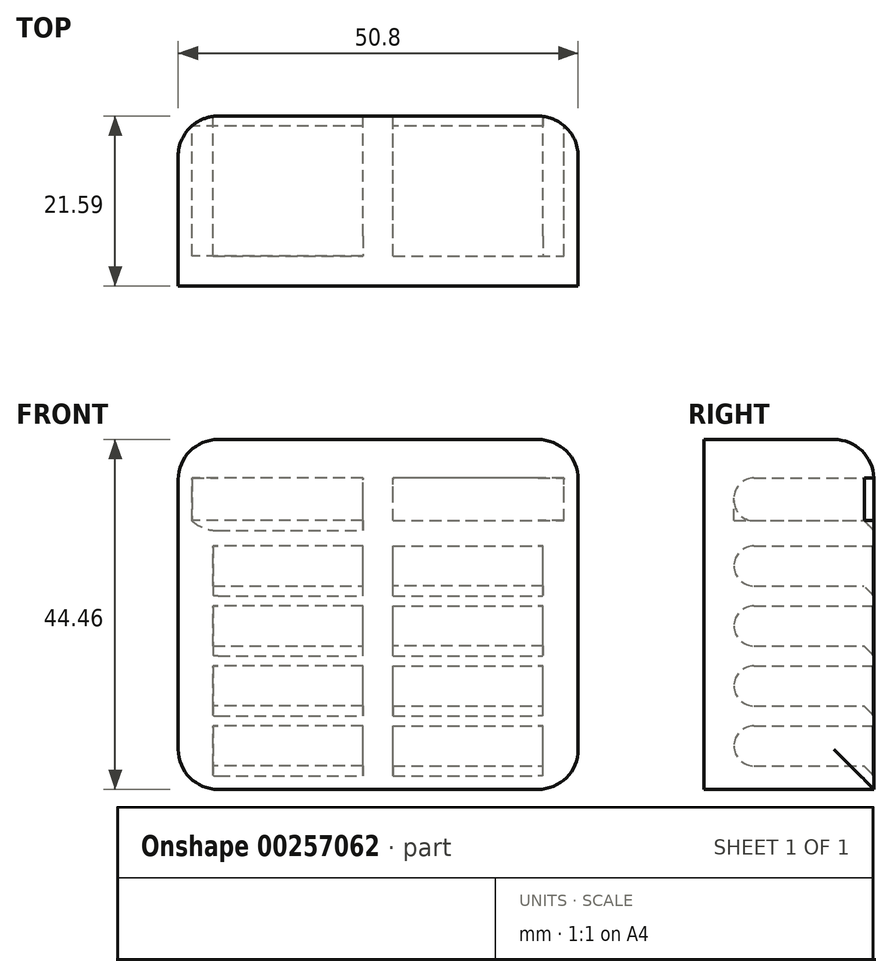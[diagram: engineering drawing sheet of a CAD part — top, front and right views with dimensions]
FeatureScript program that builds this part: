
annotation { "Feature Type Name" : "Feature", "Feature Type Description" : "" }
export const myFeature = defineFeature(function(context is Context, id is Id, definition is map)
    precondition{}
    {
        {
            var Q0;
            Q0=qCreatedBy(makeId("Front.planeOp"),FACE);
            var sketch = newSketch(context, id + "F0", { "sketchPlane" : qUnion([Q0])});
            skLineSegment(sketch, "E0.bottom", {"start": v(-25.4, -22.23) * mm, "end": v(25.4, -22.23) * mm});
            skLineSegment(sketch, "E0.top", {"start": v(-25.4, 22.23) * mm, "end": v(25.4, 22.23) * mm});
            skLineSegment(sketch, "E0.left", {"start": v(-25.4, -22.22) * mm, "end": v(-25.4, 22.22) * mm});
            skLineSegment(sketch, "E0.right", {"start": v(25.4, -22.23) * mm, "end": v(25.4, 22.22) * mm});
            skPoint(sketch, "E0.middle", {"position": v(0, 0) * mm});
            skLineSegment(sketch, "E1", {"start": v(-1.92, -19.23) * mm, "end": v(-1.92, -14.15) * mm});
            skLineSegment(sketch, "E2", {"start": v(-20.97, -19.23) * mm, "end": v(-20.97, -14.15) * mm});
            skLineSegment(sketch, "E3", {"start": v(-20.97, 3.63) * mm, "end": v(-1.92, 3.63) * mm});
            skLineSegment(sketch, "E4", {"start": v(-20.97, -4) * mm, "end": v(-1.92, -4) * mm});
            skLineSegment(sketch, "E5", {"start": v(-1.92, 1.09) * mm, "end": v(-20.97, 1.09) * mm});
            skLineSegment(sketch, "E6", {"start": v(-1.92, 8.7) * mm, "end": v(-20.97, 8.7) * mm});
            skLineSegment(sketch, "E7", {"start": v(-1.92, -6.53) * mm, "end": v(-20.97, -6.53) * mm});
            skLineSegment(sketch, "E8", {"start": v(-1.92, -11.61) * mm, "end": v(-20.97, -11.61) * mm});
            skLineSegment(sketch, "E9", {"start": v(-1.92, -14.15) * mm, "end": v(-20.97, -14.15) * mm});
            skLineSegment(sketch, "E10", {"start": v(-1.92, -19.23) * mm, "end": v(-20.97, -19.23) * mm});
            skLineSegment(sketch, "E11.MirrorCS", {"start": v(20.97, 3.63) * mm, "end": v(1.92, 3.63) * mm});
            skLineSegment(sketch, "E12.MirrorCS", {"start": v(1.92, 8.7) * mm, "end": v(20.97, 8.7) * mm});
            skLineSegment(sketch, "E13.MirrorCS", {"start": v(1.92, -19.23) * mm, "end": v(1.92, -14.15) * mm});
            skLineSegment(sketch, "E14.MirrorCS", {"start": v(20.97, -19.23) * mm, "end": v(20.97, -14.15) * mm});
            skLineSegment(sketch, "E15.MirrorCS", {"start": v(1.92, 1.09) * mm, "end": v(20.97, 1.09) * mm});
            skLineSegment(sketch, "E16.MirrorCS", {"start": v(20.97, -4) * mm, "end": v(1.92, -4) * mm});
            skLineSegment(sketch, "E17.MirrorCS", {"start": v(1.92, -6.53) * mm, "end": v(20.97, -6.53) * mm});
            skLineSegment(sketch, "E18.MirrorCS", {"start": v(1.92, -11.61) * mm, "end": v(20.97, -11.61) * mm});
            skLineSegment(sketch, "E19.MirrorCS", {"start": v(1.92, -14.15) * mm, "end": v(20.97, -14.15) * mm});
            skLineSegment(sketch, "E20.MirrorCS", {"start": v(1.92, -19.23) * mm, "end": v(20.97, -19.23) * mm});
            skLineSegment(sketch, "E21.trimOffspring", {"start": v(-1.92, 3.63) * mm, "end": v(-1.92, 8.7) * mm});
            skLineSegment(sketch, "E22.trimOffspring", {"start": v(-20.97, 3.63) * mm, "end": v(-20.97, 8.7) * mm});
            skLineSegment(sketch, "E23.trimOffspring", {"start": v(-20.97, -4) * mm, "end": v(-20.97, 1.09) * mm});
            skLineSegment(sketch, "E24.trimOffspring", {"start": v(-1.92, -4) * mm, "end": v(-1.92, 1.09) * mm});
            skLineSegment(sketch, "E25.trimOffspring", {"start": v(-1.92, -11.61) * mm, "end": v(-1.92, -6.53) * mm});
            skLineSegment(sketch, "E26.trimOffspring", {"start": v(-20.97, -11.61) * mm, "end": v(-20.97, -6.53) * mm});
            skLineSegment(sketch, "E27.trimOffspring", {"start": v(1.92, -11.61) * mm, "end": v(1.92, -6.53) * mm});
            skLineSegment(sketch, "E28.trimOffspring", {"start": v(20.97, -11.61) * mm, "end": v(20.97, -6.53) * mm});
            skLineSegment(sketch, "E29.trimOffspring", {"start": v(20.97, -4) * mm, "end": v(20.97, 1.09) * mm});
            skLineSegment(sketch, "E30.trimOffspring", {"start": v(1.92, -4) * mm, "end": v(1.92, 1.09) * mm});
            skLineSegment(sketch, "E31.trimOffspring", {"start": v(1.92, 3.63) * mm, "end": v(1.92, 8.7) * mm});
            skLineSegment(sketch, "E32.trimOffspring", {"start": v(20.97, 3.63) * mm, "end": v(20.97, 8.7) * mm});
            skLineSegment(sketch, "E33", {"start": v(1.92, 11.92) * mm, "end": v(1.92, 17.33) * mm});
            skLineSegment(sketch, "E34", {"start": v(-1.92, 11.92) * mm, "end": v(-1.92, 17.33) * mm});
            skLineSegment(sketch, "E35.bottom", {"start": v(1.92, 11.92) * mm, "end": v(23.61, 11.92) * mm});
            skLineSegment(sketch, "E35.right", {"start": v(23.61, 11.92) * mm, "end": v(23.61, 17.33) * mm});
            skLineSegment(sketch, "E36", {"start": v(23.61, 17.33) * mm, "end": v(1.92, 17.33) * mm});
            skLineSegment(sketch, "E37", {"start": v(23.61, 11.92) * mm, "end": v(1.92, 11.92) * mm});
            skLineSegment(sketch, "E38.MirrorCS", {"start": v(-23.61, 11.92) * mm, "end": v(-23.61, 17.33) * mm});
            skLineSegment(sketch, "E39.trimOffspring", {"start": v(-1.92, 11.92) * mm, "end": v(-23.61, 11.92) * mm});
            skLineSegment(sketch, "E40.trimOffspring", {"start": v(-1.92, 17.33) * mm, "end": v(-23.61, 17.33) * mm});
            skSolve(sketch);
        }
        {
            var Q0;
            Q0=makeQuery(id+"F0.imprint","IMPRINT",FACE,{"disambiguationData":[TD([[makeQuery(id+"F0.imprint","IMPRINT",EDGE,{"derivedFrom":sQuery(id+"F0.wireOp",EDGE,"E0.bottom")}),1.0]])]});
            extrude(context, id + "F1", {"entities" : qUnion([Q0]), "endBound" : BoundingType.SYMMETRIC, "depth" : 21.59 * mm, "hasSecondDirection" : true, "secondDirectionOppositeDirection" : false, "secondDirectionDepth" : 30.23 * mm});
        }
        {
            var Q0;
            Q0=makeQuery(id+"F1.opExtrude","CAP_FACE",FACE,{"disambiguationData":[OSD([sQuery(id+"F0.wireOp",EDGE,"E0.bottom"),sQuery(id+"F0.wireOp",EDGE,"E0.top"),sQuery(id+"F0.wireOp",EDGE,"E0.left"),sQuery(id+"F0.wireOp",EDGE,"E0.right"),sQuery(id+"F0.wireOp",EDGE,"E1"),sQuery(id+"F0.wireOp",EDGE,"E2"),sQuery(id+"F0.wireOp",EDGE,"E3"),sQuery(id+"F0.wireOp",EDGE,"E4"),sQuery(id+"F0.wireOp",EDGE,"E5"),sQuery(id+"F0.wireOp",EDGE,"E6"),sQuery(id+"F0.wireOp",EDGE,"E7"),sQuery(id+"F0.wireOp",EDGE,"E8"),sQuery(id+"F0.wireOp",EDGE,"E9"),sQuery(id+"F0.wireOp",EDGE,"E10"),sQuery(id+"F0.wireOp",EDGE,"E11.MirrorCS"),sQuery(id+"F0.wireOp",EDGE,"E12.MirrorCS"),sQuery(id+"F0.wireOp",EDGE,"E13.MirrorCS"),sQuery(id+"F0.wireOp",EDGE,"E14.MirrorCS"),sQuery(id+"F0.wireOp",EDGE,"E15.MirrorCS"),sQuery(id+"F0.wireOp",EDGE,"E16.MirrorCS"),sQuery(id+"F0.wireOp",EDGE,"E17.MirrorCS"),sQuery(id+"F0.wireOp",EDGE,"E18.MirrorCS"),sQuery(id+"F0.wireOp",EDGE,"E19.MirrorCS"),sQuery(id+"F0.wireOp",EDGE,"E20.MirrorCS"),sQuery(id+"F0.wireOp",EDGE,"E21.trimOffspring"),sQuery(id+"F0.wireOp",EDGE,"E22.trimOffspring"),sQuery(id+"F0.wireOp",EDGE,"E23.trimOffspring"),sQuery(id+"F0.wireOp",EDGE,"E24.trimOffspring"),sQuery(id+"F0.wireOp",EDGE,"E25.trimOffspring"),sQuery(id+"F0.wireOp",EDGE,"E26.trimOffspring"),sQuery(id+"F0.wireOp",EDGE,"E27.trimOffspring"),sQuery(id+"F0.wireOp",EDGE,"E28.trimOffspring"),sQuery(id+"F0.wireOp",EDGE,"E29.trimOffspring"),sQuery(id+"F0.wireOp",EDGE,"E30.trimOffspring"),sQuery(id+"F0.wireOp",EDGE,"E31.trimOffspring"),sQuery(id+"F0.wireOp",EDGE,"E32.trimOffspring"),sQuery(id+"F0.wireOp",EDGE,"E34"),sQuery(id+"F0.wireOp",EDGE,"E33"),sQuery(id+"F0.wireOp",EDGE,"E35.right"),sQuery(id+"F0.wireOp",EDGE,"E36"),sQuery(id+"F0.wireOp",EDGE,"E37"),sQuery(id+"F0.wireOp",EDGE,"E38.MirrorCS"),sQuery(id+"F0.wireOp",EDGE,"E39.trimOffspring"),sQuery(id+"F0.wireOp",EDGE,"E40.trimOffspring")])],"isStart":false});
            var sketch = newSketch(context, id + "F2", { "sketchPlane" : qUnion([Q0])});
            skLineSegment(sketch, "E41.bottom", {"start": v(-25.4, 22.22) * mm, "end": v(25.4, 22.22) * mm});
            skLineSegment(sketch, "E41.top", {"start": v(-25.4, -22.23) * mm, "end": v(25.4, -22.23) * mm});
            skLineSegment(sketch, "E41.left", {"start": v(-25.4, 22.22) * mm, "end": v(-25.4, -22.23) * mm});
            skLineSegment(sketch, "E41.right", {"start": v(25.4, 22.22) * mm, "end": v(25.4, -22.23) * mm});
            skSolve(sketch);
        }
        {
            var Q0;
            Q0 = qSketchRegion(id + "F2", true);
            extrude(context, id + "F3", {"entities" : qUnion([Q0]), "operationType" : NewBodyOperationType.ADD, "oppositeDirection" : true, "depth" : 3.8 * mm});
        }
        {
            var Q0;
            Q0=makeQuery(id+"F1.opExtrude","SWEPT_EDGE",EDGE,{"disambiguationData":[OSD([sQuery(id+"F0.wireOp",EDGE,"E0.top"),sQuery(id+"F0.wireOp",EDGE,"E0.right")])]});
            var Q1;
            Q1=makeQuery(id+"F1.opExtrude","SWEPT_EDGE",EDGE,{"disambiguationData":[OSD([sQuery(id+"F0.wireOp",EDGE,"E0.top"),sQuery(id+"F0.wireOp",EDGE,"E0.left")])]});
            fillet(context, id + "F4", {"entities" : qUnion([Q0, Q1]), "radius" : 5.08 * mm, "tangentPropagation" : true, "allowEdgeOverflow" : false});
        }
        {
            var Q0;
            Q0=makeQuery(id+"F1.opExtrude","CAP_EDGE",EDGE,{"disambiguationData":[OSD([sQuery(id+"F0.wireOp",EDGE,"E37")])],"isStart":true});
            var Q1;
            Q1=makeQuery(id+"F1.opExtrude","CAP_EDGE",EDGE,{"disambiguationData":[OSD([sQuery(id+"F0.wireOp",EDGE,"E39.trimOffspring")])],"isStart":true});
            var Q2;
            Q2=makeQuery(id+"F1.opExtrude","CAP_EDGE",EDGE,{"disambiguationData":[OSD([sQuery(id+"F0.wireOp",EDGE,"E3")])],"isStart":true});
            var Q3;
            Q3=makeQuery(id+"F1.opExtrude","CAP_EDGE",EDGE,{"disambiguationData":[OSD([sQuery(id+"F0.wireOp",EDGE,"E11.MirrorCS")])],"isStart":true});
            var Q4;
            Q4=makeQuery(id+"F1.opExtrude","CAP_EDGE",EDGE,{"disambiguationData":[OSD([sQuery(id+"F0.wireOp",EDGE,"E16.MirrorCS")])],"isStart":true});
            var Q5;
            Q5=makeQuery(id+"F1.opExtrude","CAP_EDGE",EDGE,{"disambiguationData":[OSD([sQuery(id+"F0.wireOp",EDGE,"E4")])],"isStart":true});
            var Q6;
            Q6=makeQuery(id+"F1.opExtrude","CAP_EDGE",EDGE,{"disambiguationData":[OSD([sQuery(id+"F0.wireOp",EDGE,"E8")])],"isStart":true});
            var Q7;
            Q7=makeQuery(id+"F1.opExtrude","CAP_EDGE",EDGE,{"disambiguationData":[OSD([sQuery(id+"F0.wireOp",EDGE,"E18.MirrorCS")])],"isStart":true});
            var Q8;
            Q8=makeQuery(id+"F1.opExtrude","CAP_EDGE",EDGE,{"disambiguationData":[OSD([sQuery(id+"F0.wireOp",EDGE,"E20.MirrorCS")])],"isStart":true});
            var Q9;
            Q9=makeQuery(id+"F1.opExtrude","CAP_EDGE",EDGE,{"disambiguationData":[OSD([sQuery(id+"F0.wireOp",EDGE,"E10")])],"isStart":true});
            chamfer(context, id + "F5", {"entities" : qUnion([Q0, Q1, Q2, Q3, Q4, Q5, Q6, Q7, Q8, Q9]), "width" : 1.27 * mm, "tangentPropagation" : true});
        }
        {
            var Q0;
            Q0=makeQuery(id+"F3.boolean.opBoolean","INTERSECT",EDGE,{"derivedFrom":[makeQuery(id+"F1.opExtrude","SWEPT_FACE",FACE,{"disambiguationData":[OSD([sQuery(id+"F0.wireOp",EDGE,"E11.MirrorCS")])]}),makeQuery(id+"F3.opExtrude","CAP_FACE",FACE,{"disambiguationData":[OSD([sQuery(id+"F2.wireOp",EDGE,"E41.bottom"),sQuery(id+"F2.wireOp",EDGE,"E41.top"),sQuery(id+"F2.wireOp",EDGE,"E41.left"),sQuery(id+"F2.wireOp",EDGE,"E41.right")])],"isStart":false})]});
            var Q1;
            Q1=makeQuery(id+"F3.boolean.opBoolean","INTERSECT",EDGE,{"derivedFrom":[makeQuery(id+"F1.opExtrude","SWEPT_FACE",FACE,{"disambiguationData":[OSD([sQuery(id+"F0.wireOp",EDGE,"E3")])]}),makeQuery(id+"F3.opExtrude","CAP_FACE",FACE,{"disambiguationData":[OSD([sQuery(id+"F2.wireOp",EDGE,"E41.bottom"),sQuery(id+"F2.wireOp",EDGE,"E41.top"),sQuery(id+"F2.wireOp",EDGE,"E41.left"),sQuery(id+"F2.wireOp",EDGE,"E41.right")])],"isStart":false})]});
            var Q2;
            Q2=makeQuery(id+"F3.boolean.opBoolean","INTERSECT",EDGE,{"derivedFrom":[makeQuery(id+"F1.opExtrude","SWEPT_FACE",FACE,{"disambiguationData":[OSD([sQuery(id+"F0.wireOp",EDGE,"E39.trimOffspring")])]}),makeQuery(id+"F3.opExtrude","CAP_FACE",FACE,{"disambiguationData":[OSD([sQuery(id+"F2.wireOp",EDGE,"E41.bottom"),sQuery(id+"F2.wireOp",EDGE,"E41.top"),sQuery(id+"F2.wireOp",EDGE,"E41.left"),sQuery(id+"F2.wireOp",EDGE,"E41.right")])],"isStart":false})]});
            var Q3;
            Q3=makeQuery(id+"F3.boolean.opBoolean","INTERSECT",EDGE,{"derivedFrom":[makeQuery(id+"F1.opExtrude","SWEPT_FACE",FACE,{"disambiguationData":[OSD([sQuery(id+"F0.wireOp",EDGE,"E37")])]}),makeQuery(id+"F3.opExtrude","CAP_FACE",FACE,{"disambiguationData":[OSD([sQuery(id+"F2.wireOp",EDGE,"E41.bottom"),sQuery(id+"F2.wireOp",EDGE,"E41.top"),sQuery(id+"F2.wireOp",EDGE,"E41.left"),sQuery(id+"F2.wireOp",EDGE,"E41.right")])],"isStart":false})]});
            var Q4;
            Q4=makeQuery(id+"F3.boolean.opBoolean","INTERSECT",EDGE,{"derivedFrom":[makeQuery(id+"F1.opExtrude","SWEPT_FACE",FACE,{"disambiguationData":[OSD([sQuery(id+"F0.wireOp",EDGE,"E16.MirrorCS")])]}),makeQuery(id+"F3.opExtrude","CAP_FACE",FACE,{"disambiguationData":[OSD([sQuery(id+"F2.wireOp",EDGE,"E41.bottom"),sQuery(id+"F2.wireOp",EDGE,"E41.top"),sQuery(id+"F2.wireOp",EDGE,"E41.left"),sQuery(id+"F2.wireOp",EDGE,"E41.right")])],"isStart":false})]});
            var Q5;
            Q5=makeQuery(id+"F3.boolean.opBoolean","INTERSECT",EDGE,{"derivedFrom":[makeQuery(id+"F1.opExtrude","SWEPT_FACE",FACE,{"disambiguationData":[OSD([sQuery(id+"F0.wireOp",EDGE,"E4")])]}),makeQuery(id+"F3.opExtrude","CAP_FACE",FACE,{"disambiguationData":[OSD([sQuery(id+"F2.wireOp",EDGE,"E41.bottom"),sQuery(id+"F2.wireOp",EDGE,"E41.top"),sQuery(id+"F2.wireOp",EDGE,"E41.left"),sQuery(id+"F2.wireOp",EDGE,"E41.right")])],"isStart":false})]});
            var Q6;
            Q6=makeQuery(id+"F3.boolean.opBoolean","INTERSECT",EDGE,{"derivedFrom":[makeQuery(id+"F1.opExtrude","SWEPT_FACE",FACE,{"disambiguationData":[OSD([sQuery(id+"F0.wireOp",EDGE,"E18.MirrorCS")])]}),makeQuery(id+"F3.opExtrude","CAP_FACE",FACE,{"disambiguationData":[OSD([sQuery(id+"F2.wireOp",EDGE,"E41.bottom"),sQuery(id+"F2.wireOp",EDGE,"E41.top"),sQuery(id+"F2.wireOp",EDGE,"E41.left"),sQuery(id+"F2.wireOp",EDGE,"E41.right")])],"isStart":false})]});
            var Q7;
            Q7=makeQuery(id+"F3.boolean.opBoolean","INTERSECT",EDGE,{"derivedFrom":[makeQuery(id+"F1.opExtrude","SWEPT_FACE",FACE,{"disambiguationData":[OSD([sQuery(id+"F0.wireOp",EDGE,"E8")])]}),makeQuery(id+"F3.opExtrude","CAP_FACE",FACE,{"disambiguationData":[OSD([sQuery(id+"F2.wireOp",EDGE,"E41.bottom"),sQuery(id+"F2.wireOp",EDGE,"E41.top"),sQuery(id+"F2.wireOp",EDGE,"E41.left"),sQuery(id+"F2.wireOp",EDGE,"E41.right")])],"isStart":false})]});
            var Q8;
            Q8=makeQuery(id+"F3.boolean.opBoolean","INTERSECT",EDGE,{"derivedFrom":[makeQuery(id+"F1.opExtrude","SWEPT_FACE",FACE,{"disambiguationData":[OSD([sQuery(id+"F0.wireOp",EDGE,"E20.MirrorCS")])]}),makeQuery(id+"F3.opExtrude","CAP_FACE",FACE,{"disambiguationData":[OSD([sQuery(id+"F2.wireOp",EDGE,"E41.bottom"),sQuery(id+"F2.wireOp",EDGE,"E41.top"),sQuery(id+"F2.wireOp",EDGE,"E41.left"),sQuery(id+"F2.wireOp",EDGE,"E41.right")])],"isStart":false})]});
            var Q9;
            Q9=makeQuery(id+"F3.boolean.opBoolean","INTERSECT",EDGE,{"derivedFrom":[makeQuery(id+"F1.opExtrude","SWEPT_FACE",FACE,{"disambiguationData":[OSD([sQuery(id+"F0.wireOp",EDGE,"E10")])]}),makeQuery(id+"F3.opExtrude","CAP_FACE",FACE,{"disambiguationData":[OSD([sQuery(id+"F2.wireOp",EDGE,"E41.bottom"),sQuery(id+"F2.wireOp",EDGE,"E41.top"),sQuery(id+"F2.wireOp",EDGE,"E41.left"),sQuery(id+"F2.wireOp",EDGE,"E41.right")])],"isStart":false})]});
            fillet(context, id + "F6", {"entities" : qUnion([Q0, Q1, Q2, Q3, Q4, Q5, Q6, Q7, Q8, Q9]), "radius" : 2.54 * mm, "tangentPropagation" : true, "allowEdgeOverflow" : false});
        }
        {
            var Q0;
            Q0=makeQuery(id+"F3.boolean.opBoolean","INTERSECT",EDGE,{"derivedFrom":[makeQuery(id+"F1.opExtrude","SWEPT_FACE",FACE,{"disambiguationData":[OSD([sQuery(id+"F0.wireOp",EDGE,"E15.MirrorCS")])]}),makeQuery(id+"F3.opExtrude","CAP_FACE",FACE,{"disambiguationData":[OSD([sQuery(id+"F2.wireOp",EDGE,"E41.bottom"),sQuery(id+"F2.wireOp",EDGE,"E41.top"),sQuery(id+"F2.wireOp",EDGE,"E41.left"),sQuery(id+"F2.wireOp",EDGE,"E41.right")])],"isStart":false})]});
            var Q1;
            Q1=makeQuery(id+"F3.boolean.opBoolean","INTERSECT",EDGE,{"derivedFrom":[makeQuery(id+"F1.opExtrude","SWEPT_FACE",FACE,{"disambiguationData":[OSD([sQuery(id+"F0.wireOp",EDGE,"E12.MirrorCS")])]}),makeQuery(id+"F3.opExtrude","CAP_FACE",FACE,{"disambiguationData":[OSD([sQuery(id+"F2.wireOp",EDGE,"E41.bottom"),sQuery(id+"F2.wireOp",EDGE,"E41.top"),sQuery(id+"F2.wireOp",EDGE,"E41.left"),sQuery(id+"F2.wireOp",EDGE,"E41.right")])],"isStart":false})]});
            var Q2;
            Q2=makeQuery(id+"F3.boolean.opBoolean","INTERSECT",EDGE,{"derivedFrom":[makeQuery(id+"F1.opExtrude","SWEPT_FACE",FACE,{"disambiguationData":[OSD([sQuery(id+"F0.wireOp",EDGE,"E6")])]}),makeQuery(id+"F3.opExtrude","CAP_FACE",FACE,{"disambiguationData":[OSD([sQuery(id+"F2.wireOp",EDGE,"E41.bottom"),sQuery(id+"F2.wireOp",EDGE,"E41.top"),sQuery(id+"F2.wireOp",EDGE,"E41.left"),sQuery(id+"F2.wireOp",EDGE,"E41.right")])],"isStart":false})]});
            var Q3;
            Q3=makeQuery(id+"F3.boolean.opBoolean","INTERSECT",EDGE,{"derivedFrom":[makeQuery(id+"F1.opExtrude","SWEPT_FACE",FACE,{"disambiguationData":[OSD([sQuery(id+"F0.wireOp",EDGE,"E5")])]}),makeQuery(id+"F3.opExtrude","CAP_FACE",FACE,{"disambiguationData":[OSD([sQuery(id+"F2.wireOp",EDGE,"E41.bottom"),sQuery(id+"F2.wireOp",EDGE,"E41.top"),sQuery(id+"F2.wireOp",EDGE,"E41.left"),sQuery(id+"F2.wireOp",EDGE,"E41.right")])],"isStart":false})]});
            var Q4;
            Q4=makeQuery(id+"F3.boolean.opBoolean","INTERSECT",EDGE,{"derivedFrom":[makeQuery(id+"F1.opExtrude","SWEPT_FACE",FACE,{"disambiguationData":[OSD([sQuery(id+"F0.wireOp",EDGE,"E7")])]}),makeQuery(id+"F3.opExtrude","CAP_FACE",FACE,{"disambiguationData":[OSD([sQuery(id+"F2.wireOp",EDGE,"E41.bottom"),sQuery(id+"F2.wireOp",EDGE,"E41.top"),sQuery(id+"F2.wireOp",EDGE,"E41.left"),sQuery(id+"F2.wireOp",EDGE,"E41.right")])],"isStart":false})]});
            var Q5;
            Q5=makeQuery(id+"F3.boolean.opBoolean","INTERSECT",EDGE,{"derivedFrom":[makeQuery(id+"F1.opExtrude","SWEPT_FACE",FACE,{"disambiguationData":[OSD([sQuery(id+"F0.wireOp",EDGE,"E17.MirrorCS")])]}),makeQuery(id+"F3.opExtrude","CAP_FACE",FACE,{"disambiguationData":[OSD([sQuery(id+"F2.wireOp",EDGE,"E41.bottom"),sQuery(id+"F2.wireOp",EDGE,"E41.top"),sQuery(id+"F2.wireOp",EDGE,"E41.left"),sQuery(id+"F2.wireOp",EDGE,"E41.right")])],"isStart":false})]});
            var Q6;
            Q6=makeQuery(id+"F3.boolean.opBoolean","INTERSECT",EDGE,{"derivedFrom":[makeQuery(id+"F1.opExtrude","SWEPT_FACE",FACE,{"disambiguationData":[OSD([sQuery(id+"F0.wireOp",EDGE,"E40.trimOffspring")])]}),makeQuery(id+"F3.opExtrude","CAP_FACE",FACE,{"disambiguationData":[OSD([sQuery(id+"F2.wireOp",EDGE,"E41.bottom"),sQuery(id+"F2.wireOp",EDGE,"E41.top"),sQuery(id+"F2.wireOp",EDGE,"E41.left"),sQuery(id+"F2.wireOp",EDGE,"E41.right")])],"isStart":false})]});
            var Q7;
            Q7=makeQuery(id+"F3.boolean.opBoolean","INTERSECT",EDGE,{"derivedFrom":[makeQuery(id+"F1.opExtrude","SWEPT_FACE",FACE,{"disambiguationData":[OSD([sQuery(id+"F0.wireOp",EDGE,"E36")])]}),makeQuery(id+"F3.opExtrude","CAP_FACE",FACE,{"disambiguationData":[OSD([sQuery(id+"F2.wireOp",EDGE,"E41.bottom"),sQuery(id+"F2.wireOp",EDGE,"E41.top"),sQuery(id+"F2.wireOp",EDGE,"E41.left"),sQuery(id+"F2.wireOp",EDGE,"E41.right")])],"isStart":false})]});
            var Q8;
            Q8=makeQuery(id+"F3.boolean.opBoolean","INTERSECT",EDGE,{"derivedFrom":[makeQuery(id+"F1.opExtrude","SWEPT_FACE",FACE,{"disambiguationData":[OSD([sQuery(id+"F0.wireOp",EDGE,"E19.MirrorCS")])]}),makeQuery(id+"F3.opExtrude","CAP_FACE",FACE,{"disambiguationData":[OSD([sQuery(id+"F2.wireOp",EDGE,"E41.bottom"),sQuery(id+"F2.wireOp",EDGE,"E41.top"),sQuery(id+"F2.wireOp",EDGE,"E41.left"),sQuery(id+"F2.wireOp",EDGE,"E41.right")])],"isStart":false})]});
            var Q9;
            Q9=makeQuery(id+"F3.boolean.opBoolean","INTERSECT",EDGE,{"derivedFrom":[makeQuery(id+"F1.opExtrude","SWEPT_FACE",FACE,{"disambiguationData":[OSD([sQuery(id+"F0.wireOp",EDGE,"E9")])]}),makeQuery(id+"F3.opExtrude","CAP_FACE",FACE,{"disambiguationData":[OSD([sQuery(id+"F2.wireOp",EDGE,"E41.bottom"),sQuery(id+"F2.wireOp",EDGE,"E41.top"),sQuery(id+"F2.wireOp",EDGE,"E41.left"),sQuery(id+"F2.wireOp",EDGE,"E41.right")])],"isStart":false})]});
            fillet(context, id + "F7", {"entities" : qUnion([Q0, Q1, Q2, Q3, Q4, Q5, Q6, Q7, Q8, Q9]), "radius" : 2.54 * mm, "tangentPropagation" : true, "allowEdgeOverflow" : false});
        }
        {
            var Q0;
            Q0=makeQuery(id+"F1.opExtrude","CAP_EDGE",EDGE,{"disambiguationData":[OSD([sQuery(id+"F0.wireOp",EDGE,"E0.right")])],"isStart":true});
            var Q1;
            Q1=makeQuery(id+"F1.opExtrude","CAP_EDGE",EDGE,{"disambiguationData":[OSD([sQuery(id+"F0.wireOp",EDGE,"E0.left")])],"isStart":true});
            var Q2;
            Q2=makeQuery(id+"F1.opExtrude","SWEPT_EDGE",EDGE,{"disambiguationData":[OSD([sQuery(id+"F0.wireOp",EDGE,"E0.bottom"),sQuery(id+"F0.wireOp",EDGE,"E0.left")])]});
            var Q3;
            Q3=makeQuery(id+"F1.opExtrude","SWEPT_EDGE",EDGE,{"disambiguationData":[OSD([sQuery(id+"F0.wireOp",EDGE,"E0.bottom"),sQuery(id+"F0.wireOp",EDGE,"E0.right")])]});
            fillet(context, id + "F8", {"entities" : qUnion([Q0, Q1, Q2, Q3]), "radius" : 5.08 * mm, "tangentPropagation" : true, "allowEdgeOverflow" : false});
        }
    });
